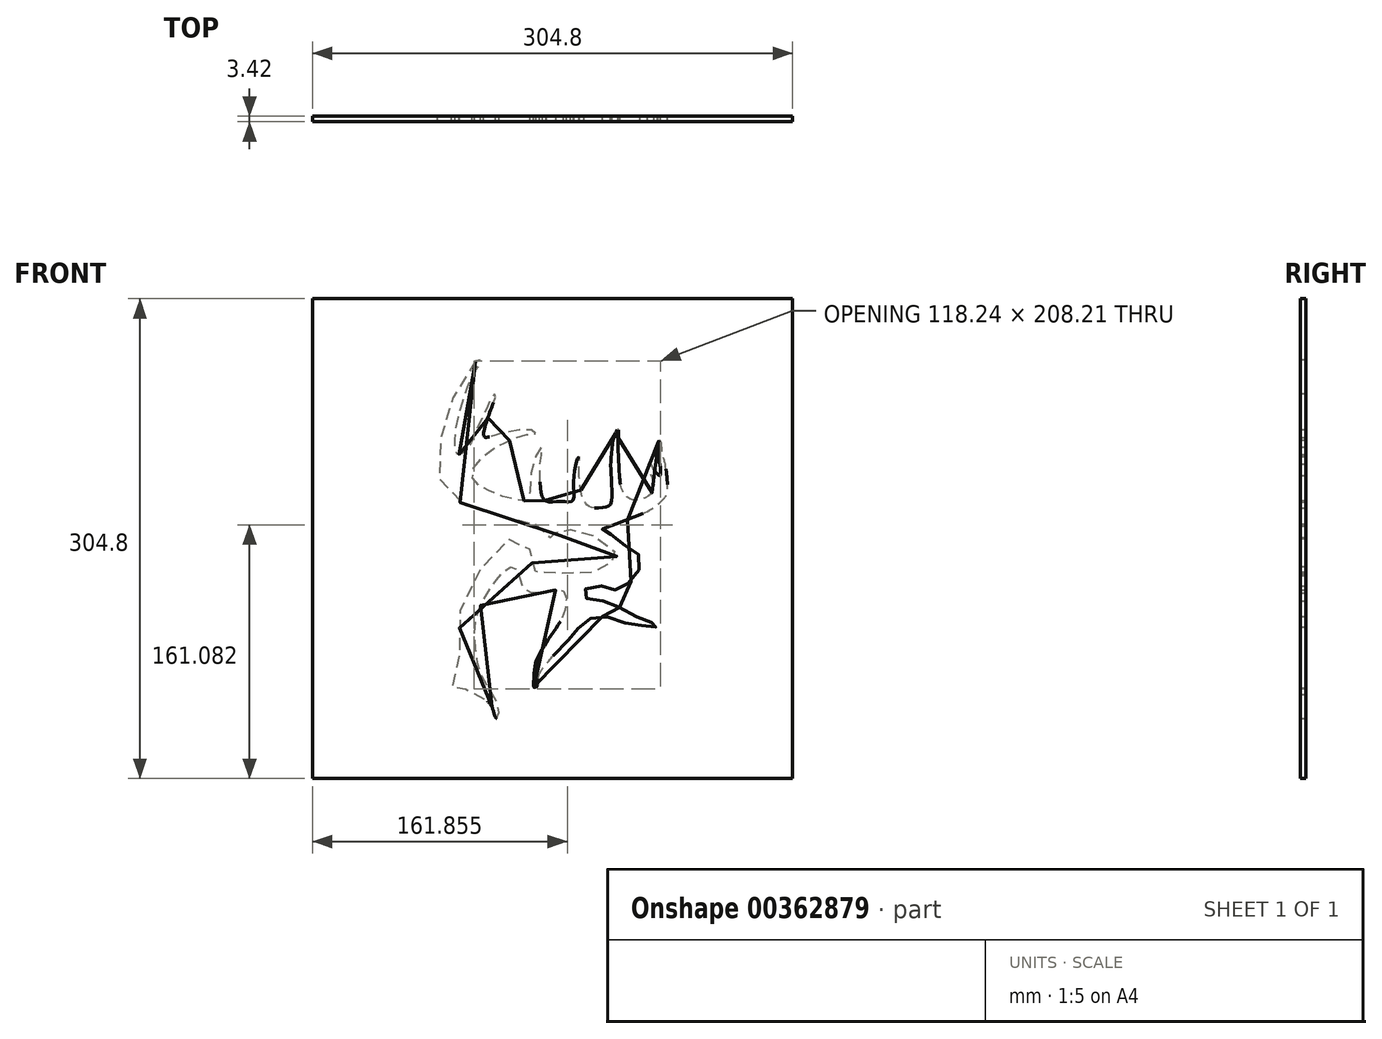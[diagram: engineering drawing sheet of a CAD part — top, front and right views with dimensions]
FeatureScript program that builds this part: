
annotation { "Feature Type Name" : "Feature", "Feature Type Description" : "" }
export const myFeature = defineFeature(function(context is Context, id is Id, definition is map)
    precondition{}
    {
        {
            var Q0;
            Q0=qCreatedBy(makeId("Front.planeOp"),FACE);
            var sketch = newSketch(context, id + "F0", { "sketchPlane" : qUnion([Q0])});
            skLineSegment(sketch, "E0.bottom", {"start": v(152.4, 152.4) * mm, "end": v(-152.4, 152.4) * mm});
            skLineSegment(sketch, "E0.top", {"start": v(152.4, -152.4) * mm, "end": v(-152.4, -152.4) * mm});
            skLineSegment(sketch, "E0.left", {"start": v(152.4, 152.4) * mm, "end": v(152.4, -152.4) * mm});
            skLineSegment(sketch, "E0.right", {"start": v(-152.4, 152.4) * mm, "end": v(-152.4, -152.4) * mm});
            skFitSpline(sketch, "E1", {"points": [v(-48.72, 112.79) * mm, v(-60.29, 95.34) * mm, v(-68.25, 75.62) * mm, v(-72.7, 53.05) * mm, v(-71.14, 36.07) * mm, v(-61.22, 24.57) * mm, v(-42.4, 16.8) * mm, v(-23.34, 11.27) * mm, v(-16.46, 8.57) * mm, v(-3.95, 8.57) * mm, v(-4.06, 3.15) * mm, v(2.81, 0) * mm, v(6.87, 1.12) * mm, v(2.48, 3.5) * mm, v(3.38, 5.97) * mm, v(7.89, 8.11) * mm, v(11.27, 6.54) * mm, v(11.6, 3.6) * mm, v(21.64, 2.6) * mm, v(33.25, -1.36) * mm, v(37.87, -6.43) * mm, v(40.92, -9.13) * mm, v(42.83, -10.26) * mm, v(39.87, -11.69) * mm, v(36.03, -17.83) * mm, v(32.01, -21.94) * mm, v(25.16, -21.44) * mm, v(13.97, -21.38) * mm, v(1.24, -22.73) * mm, v(-8, -22.96) * mm, v(-11.73, -19.8) * mm, v(-12.86, -16.76) * mm, v(-13.87, -8.75) * mm, v(-18.72, 0) * mm, v(-26.72, 0) * mm, v(-35.97, -7.51) * mm, v(-55.02, -33.67) * mm, v(-58.96, -50.8) * mm, v(-59.08, -73.92) * mm, v(-59.64, -82.37) * mm, v(-64.04, -97.6) * mm, v(-61.67, -98.83) * mm, v(-57.16, -96.13) * mm, v(-48.93, -95.68) * mm, v(-42.84, -101.2) * mm, v(-38, -107.85) * mm, v(-35.74, -114.17) * mm, v(-34.28, -112.25) * mm, v(-35.52, -103.46) * mm, v(-44.42, -88.35) * mm, v(-48.48, -72.57) * mm, v(-48.98, -52.9) * mm, v(-42.54, -36.5) * mm, v(-33.9, -23.99) * mm, v(-28.6, -19.06) * mm, v(-23.86, -17.92) * mm, v(-21.02, -24.18) * mm, v(-18.74, -31.29) * mm, v(-12.4, -34.42) * mm, v(-2.06, -33.37) * mm, v(6.95, -33.09) * mm, v(8.84, -38.5) * mm, v(6.38, -49.96) * mm, v(0, -59.92) * mm, v(-6.04, -69.5) * mm, v(-10.5, -78.3) * mm, v(-11.73, -86.56) * mm, v(-11.44, -94.62) * mm, v(-9.36, -92.15) * mm, v(-8.6, -86.84) * mm, v(-3.86, -79.35) * mm, v(7.8, -66.46) * mm, v(13.11, -61.34) * mm, v(17.47, -55.27) * mm, v(23.92, -50.72) * mm, v(32.92, -49.4) * mm, v(42.5, -52.24) * mm, v(51.5, -54.6) * mm, v(59.66, -55.46) * mm, v(65.34, -56.13) * mm, v(66.77, -55.37) * mm, v(64.97, -53.76) * mm, v(58.52, -52.05) * mm, v(51.6, -48.64) * mm, v(39.56, -42) * mm, v(32.17, -39.63) * mm, v(22.69, -38.87) * mm, v(20.6, -35.65) * mm, v(20.32, -32.61) * mm, v(26.76, -30.24) * mm, v(34.16, -30.53) * mm, v(39.28, -32.42) * mm, v(43.73, -30.24) * mm, v(51.4, -25.98) * mm, v(55.49, -16.97) * mm, v(54.7, -10.22) * mm, v(49.5, -6.79) * mm, v(40.89, 0) * mm, v(35.39, 3.5) * mm, v(32.26, 4.93) * mm, v(31.98, 6.92) * mm, v(38.42, 8.9) * mm, v(60.5, 17.54) * mm, v(70.18, 24.84) * mm, v(72.83, 30.24) * mm, v(72.17, 43.6) * mm, v(71.32, 48.82) * mm, v(70.4, 51.95) * mm, v(69.8, 54.7) * mm, v(69, 61.15) * mm, v(67.9, 62.56) * mm, v(67.1, 60.47) * mm, v(67.1, 55.57) * mm, v(68.5, 45.36) * mm, v(68.66, 41.24) * mm, v(68.03, 40.1) * mm, v(65.24, 42.94) * mm, v(62.9, 46.57) * mm, v(60.81, 47.5) * mm, v(60.99, 44.54) * mm, v(64.4, 35.36) * mm, v(63.92, 30.33) * mm, v(61.36, 27.4) * mm, v(53.59, 24.46) * mm, v(48.36, 25.77) * mm, v(44.64, 30) * mm, v(42.76, 38.03) * mm, v(41.64, 59.63) * mm, v(41.83, 65.93) * mm, v(41.78, 69.49) * mm, v(40.5, 67.69) * mm, v(38.8, 63.6) * mm, v(37.19, 51.2) * mm, v(37.19, 40.95) * mm, v(37.1, 22.56) * mm, v(33.3, 20) * mm, v(24.01, 20.2) * mm, v(19.65, 25.03) * mm, v(17.85, 31.57) * mm, v(16.8, 42.22) * mm, v(17.07, 49.93) * mm, v(17.1, 52.14) * mm, v(15.8, 50.47) * mm, v(13.38, 35.39) * mm, v(12.66, 23.92) * mm, v(5.8, 23.7) * mm, v(-3.48, 23.7) * mm, v(-7.18, 28.82) * mm, v(-7.84, 46.74) * mm, v(-6.9, 53.09) * mm, v(-6.6, 58.3) * mm, v(-9.93, 53.85) * mm, v(-14.2, 36.12) * mm, v(-14.95, 24.36) * mm, v(-18.65, 24.08) * mm, v(-32.1, 26.83) * mm, v(-43.58, 32.33) * mm, v(-48.7, 35.64) * mm, v(-51.07, 40.67) * mm, v(-48.6, 47.3) * mm, v(-39.6, 55.74) * mm, v(-30.02, 61.15) * mm, v(-21.2, 64.84) * mm, v(-14.67, 66.36) * mm, v(-10.59, 67.02) * mm, v(-11.06, 68.35) * mm, v(-17.04, 69.2) * mm, v(-30.12, 67.5) * mm, v(-41.87, 64.37) * mm, v(-43.58, 65.32) * mm, v(-42.25, 73.18) * mm, v(-37.8, 85.41) * mm, v(-36.61, 88.54) * mm, v(-36.28, 92.15) * mm, v(-37.8, 90.82) * mm, v(-42.73, 80.77) * mm, v(-47.84, 70.15) * mm, v(-51.45, 61.62) * mm, v(-54.58, 56.22) * mm, v(-58.75, 53.66) * mm, v(-60.93, 54.22) * mm, v(-61.97, 59.44) * mm, v(-60.45, 74.04) * mm, v(-57.25, 86.48) * mm, v(-52.68, 99.54) * mm, v(-47.94, 108.36) * mm, v(-45.95, 111.4) * mm, v(-46.04, 113.57) * mm, v(-48.72, 112.79) * mm]});
            skSolve(sketch);
        }
        {
            var Q0;
            Q0=makeQuery(id+"F0.imprint","IMPRINT",FACE,{"disambiguationData":[TD([[makeQuery(id+"F0.imprint","IMPRINT",EDGE,{"derivedFrom":sQuery(id+"F0.wireOp",EDGE,"E0.bottom")}),1.0]])]});
            extrude(context, id + "F1", {"entities" : qUnion([Q0]), "depth" : 3.42 * mm, "symmetric" : true});
        }
    });
